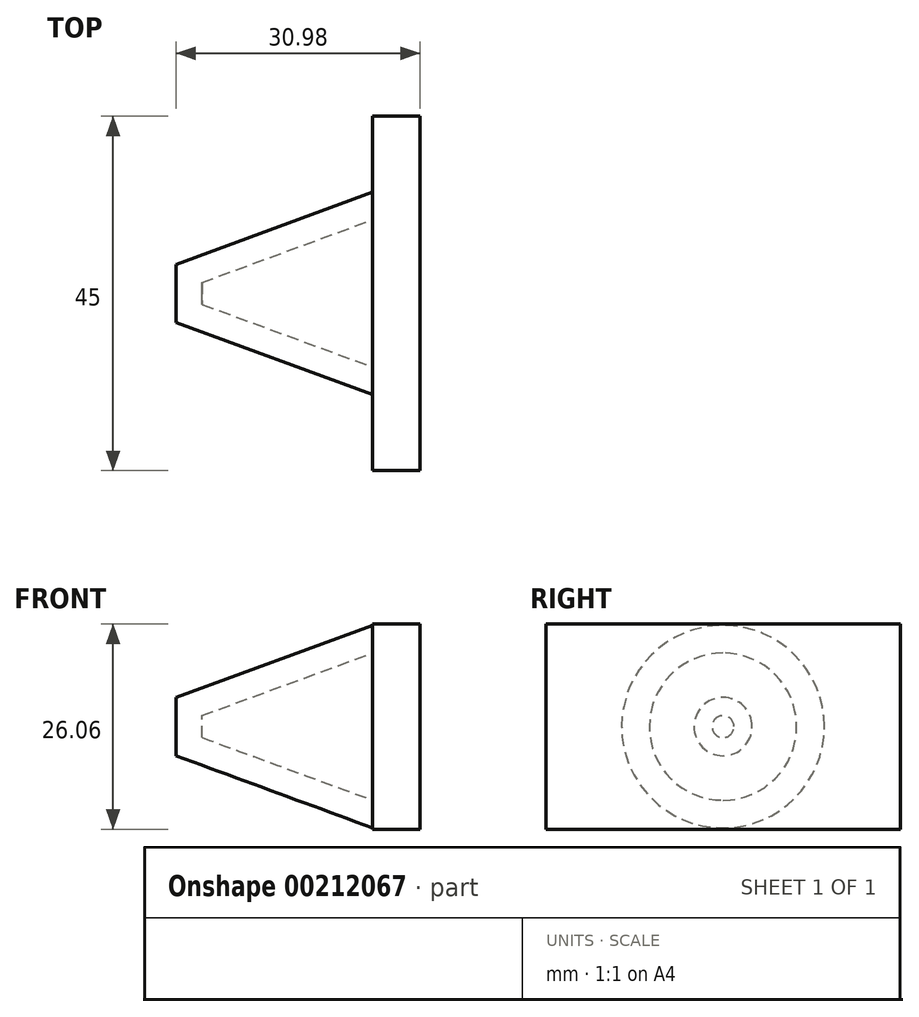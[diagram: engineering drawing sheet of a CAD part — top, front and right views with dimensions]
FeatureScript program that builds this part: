
annotation { "Feature Type Name" : "Feature", "Feature Type Description" : "" }
export const myFeature = defineFeature(function(context is Context, id is Id, definition is map)
    precondition{}
    {
        {
            var Q0;
            Q0=qCreatedBy(makeId("Front.planeOp"),FACE);
            var sketch = newSketch(context, id + "F0", { "sketchPlane" : qUnion([Q0])});
            skLineSegment(sketch, "E0", {"start": v(-21.4, 0) * mm, "end": v(-21.4, 3.7) * mm});
            skLineSegment(sketch, "E1", {"start": v(-21.4, 3.7) * mm, "end": v(3.57, 12.87) * mm});
            skLineSegment(sketch, "E2", {"start": v(3.57, 12.87) * mm, "end": v(3.57, 0) * mm});
            skLineSegment(sketch, "E3", {"start": v(3.57, 0) * mm, "end": v(-21.4, 0) * mm});
            skSolve(sketch);
        }
        {
            var Q0;
            Q0=makeQuery(id+"F0.imprint","IMPRINT",FACE,{"disambiguationData":[TD([[makeQuery(id+"F0.imprint","IMPRINT",EDGE,{"derivedFrom":sQuery(id+"F0.wireOp",EDGE,"E0")}),-1.0]])]});
            var Q1;
            Q1=sQuery(id+"F0.wireOp",EDGE,"E3");
            revolve(context, id + "F1", {"entities" : qUnion([Q0]), "axis" : qUnion([Q1]), "revolveType" : RevolveType.FULL});
        }
        {
            var Q0;
            Q0=makeQuery(id+"F1.opRevolve","SWEPT_FACE",FACE,{"disambiguationData":[OSD([sQuery(id+"F0.wireOp",EDGE,"E2")])]});
            shell(context, id + "F2", {"entities" : qUnion([Q0]), "thickness" : 3.3 * mm});
        }
        {
            var Q0;
            Q0=makeQuery(id+"F1.opRevolve","SWEPT_FACE",FACE,{"disambiguationData":[OSD([sQuery(id+"F0.wireOp",EDGE,"E2")])]});
            var sketch = newSketch(context, id + "F3", { "sketchPlane" : qUnion([Q0])});
            skLineSegment(sketch, "E4.bottom", {"start": v(22.5, 13.03) * mm, "end": v(-22.5, 13.03) * mm});
            skLineSegment(sketch, "E4.top", {"start": v(22.5, -13.03) * mm, "end": v(-22.5, -13.03) * mm});
            skLineSegment(sketch, "E4.left", {"start": v(22.5, 13.03) * mm, "end": v(22.5, -13.03) * mm});
            skLineSegment(sketch, "E4.right", {"start": v(-22.5, 13.03) * mm, "end": v(-22.5, -13.03) * mm});
            skPoint(sketch, "E4.middle", {"position": v(0, 0) * mm});
            skSolve(sketch);
        }
        {
            var Q0;
            Q0 = qSketchRegion(id + "F3", true);
            extrude(context, id + "F4", {"entities" : qUnion([Q0]), "operationType" : NewBodyOperationType.ADD, "depth" : 6 * mm});
        }
    });
